# Revit family: GT_клапан
name_source: partatom
category: Арматура воздуховодов
revit_build: Autodesk Revit 2014 (Build: 20130308_1515(x64)
units: mm (PartAtom-declared; Revit-internal decimal feet)

## types (374) — shared parameters
T = 20 мм
URL = http://inplast.ru
Изготовитель = INPLAST-SMAY
Материал = Оцинкованная сталь (INPLAST)
Описание = Щелевой клапан расхода воздуха из оцинкованной стали
zero-valued in all types: Вес, кг

## per-type parameters (varying)
| type | Aef | C | D |
| GT-75х75 | 0.003 м² | 75 мм | 75 мм |
| GT-100х100 | 0.006 м² | 100 мм | 100 мм |
| GT-125х100 | 0.008 м² | 125 мм | 100 мм |
| GT-125х125 | 0.009 м² | 125 мм | 125 мм |
| GT-150х100 | 0.009 м² | 150 мм | 100 мм |
| GT-150х125 | 0.011 м² | 150 мм | 125 мм |
| GT-150х150 | 0.014 м² | 150 мм | 150 мм |
| GT-200х100 | 0.012 м² | 200 мм | 100 мм |
| GT-200х125 | 0.015 м² | 200 мм | 125 мм |
| GT-200х150 | 0.018 м² | 200 мм | 150 мм |
| GT-200х200 | 0.024 м² | 200 мм | 200 мм |
| GT-205х205 | 0.025 м² | 205 мм | 205 мм |
| GT-225х100 | 0.014 м² | 225 мм | 100 мм |
| GT-225х125 | 0.017 м² | 225 мм | 125 мм |
| GT-225х150 | 0.020 м² | 225 мм | 150 мм |
| GT-225х200 | 0.027 м² | 225 мм | 200 мм |
| GT-225х225 | 0.030 м² | 225 мм | 225 мм |
| GT-250х100 | 0.015 м² | 250 мм | 100 мм |
| GT-250х125 | 0.019 м² | 250 мм | 125 мм |
| GT-250х150 | 0.023 м² | 250 мм | 150 мм |
| GT-250х200 | 0.030 м² | 250 мм | 200 мм |
| GT-250х225 | 0.034 м² | 250 мм | 225 мм |
| GT-250х250 | 0.038 м² | 250 мм | 250 мм |
| GT-261х261 | 0.041 м² | 261 мм | 261 мм |
| GT-300х100 | 0.018 м² | 300 мм | 100 мм |
| GT-300х125 | 0.023 м² | 300 мм | 125 мм |
| GT-300х150 | 0.027 м² | 300 мм | 150 мм |
| GT-300х200 | 0.036 м² | 300 мм | 200 мм |
| GT-300х225 | 0.041 м² | 300 мм | 225 мм |
| GT-300х250 | 0.045 м² | 300 мм | 250 мм |
| GT-300х300 | 0.054 м² | 300 мм | 300 мм |
| GT-317х317 | 0.060 м² | 317 мм | 317 мм |
| GT-325х100 | 0.020 м² | 325 мм | 100 мм |
| GT-325х125 | 0.024 м² | 325 мм | 125 мм |
| GT-325х150 | 0.029 м² | 325 мм | 150 мм |
| GT-325х200 | 0.039 м² | 325 мм | 200 мм |
| GT-325х225 | 0.044 м² | 325 мм | 225 мм |
| GT-325х250 | 0.049 м² | 325 мм | 250 мм |
| GT-325х300 | 0.059 м² | 325 мм | 300 мм |
| GT-325х325 | 0.064 м² | 325 мм | 325 мм |
| GT-350х100 | 0.021 м² | 350 мм | 100 мм |
| GT-350х125 | 0.026 м² | 350 мм | 125 мм |
| GT-350х150 | 0.032 м² | 350 мм | 150 мм |
| GT-350х200 | 0.042 м² | 350 мм | 200 мм |
| GT-350х225 | 0.047 м² | 350 мм | 225 мм |
| GT-350х250 | 0.053 м² | 350 мм | 250 мм |
| GT-350х300 | 0.063 м² | 350 мм | 300 мм |
| GT-350х325 | 0.068 м² | 350 мм | 325 мм |
| GT-350х350 | 0.074 м² | 350 мм | 350 мм |
| GT-372х372 | 0.083 м² | 372 мм | 372 мм |
| GT-400х100 | 0.024 м² | 400 мм | 100 мм |
| GT-400х125 | 0.030 м² | 400 мм | 125 мм |
| GT-400х150 | 0.036 м² | 400 мм | 150 мм |
| GT-400х200 | 0.048 м² | 400 мм | 200 мм |
| GT-400х225 | 0.054 м² | 400 мм | 225 мм |
| GT-400х250 | 0.060 м² | 400 мм | 250 мм |
| GT-400х300 | 0.072 м² | 400 мм | 300 мм |
| GT-400х325 | 0.078 м² | 400 мм | 325 мм |
| GT-400х350 | 0.084 м² | 400 мм | 350 мм |
| GT-400х400 | 0.096 м² | 400 мм | 400 мм |
| GT-425х100 | 0.026 м² | 425 мм | 100 мм |
| GT-425х125 | 0.032 м² | 425 мм | 125 мм |
| GT-425х150 | 0.038 м² | 425 мм | 150 мм |
| GT-425х200 | 0.051 м² | 425 мм | 200 мм |
| GT-425х225 | 0.058 м² | 425 мм | 225 мм |
| GT-425х250 | 0.064 м² | 425 мм | 250 мм |
| GT-425х300 | 0.077 м² | 425 мм | 300 мм |
| GT-425х325 | 0.083 м² | 425 мм | 325 мм |
| GT-425х350 | 0.089 м² | 425 мм | 350 мм |
| GT-425х400 | 0.102 м² | 425 мм | 400 мм |
| GT-425х425 | 0.109 м² | 425 мм | 425 мм |
| GT-429х429 | 0.111 м² | 429 мм | 429 мм |
| GT-450х100 | 0.027 м² | 450 мм | 100 мм |
| GT-450х125 | 0.034 м² | 450 мм | 125 мм |
| GT-450х150 | 0.041 м² | 450 мм | 150 мм |
| GT-450х200 | 0.054 м² | 450 мм | 200 мм |
| GT-450х225 | 0.061 м² | 450 мм | 225 мм |
| GT-450х250 | 0.068 м² | 450 мм | 250 мм |
| GT-450х300 | 0.081 м² | 450 мм | 300 мм |
| GT-450х325 | 0.088 м² | 450 мм | 325 мм |
| GT-450х350 | 0.095 м² | 450 мм | 350 мм |
| GT-450х400 | 0.108 м² | 450 мм | 400 мм |
| GT-450х425 | 0.115 м² | 450 мм | 425 мм |
| GT-450х450 | 0.122 м² | 450 мм | 450 мм |
| GT-458х458 | 0.126 м² | 458 мм | 458 мм |
| GT-500х100 | 0.030 м² | 500 мм | 100 мм |
| GT-500х125 | 0.038 м² | 500 мм | 125 мм |
| GT-500х150 | 0.045 м² | 500 мм | 150 мм |
| GT-500х200 | 0.060 м² | 500 мм | 200 мм |
| GT-500х225 | 0.068 м² | 500 мм | 225 мм |
| GT-500х250 | 0.075 м² | 500 мм | 250 мм |
| GT-500х300 | 0.090 м² | 500 мм | 300 мм |
| GT-500х325 | 0.098 м² | 500 мм | 325 мм |
| GT-500х350 | 0.105 м² | 500 мм | 350 мм |
| GT-500х400 | 0.120 м² | 500 мм | 400 мм |
| GT-500х425 | 0.128 м² | 500 мм | 425 мм |
| GT-500х450 | 0.135 м² | 500 мм | 450 мм |
| GT-500х500 | 0.150 м² | 500 мм | 500 мм |
| GT-525х100 | 0.032 м² | 525 мм | 100 мм |
| GT-525х125 | 0.039 м² | 525 мм | 125 мм |
| GT-525х150 | 0.047 м² | 525 мм | 150 мм |
| GT-525х200 | 0.063 м² | 525 мм | 200 мм |
| GT-525х225 | 0.071 м² | 525 мм | 225 мм |
| GT-525х250 | 0.079 м² | 525 мм | 250 мм |
| GT-525х300 | 0.095 м² | 525 мм | 300 мм |
| GT-525х325 | 0.103 м² | 525 мм | 325 мм |
| GT-525х350 | 0.111 м² | 525 мм | 350 мм |
| GT-525х400 | 0.126 м² | 525 мм | 400 мм |
| GT-525х425 | 0.134 м² | 525 мм | 425 мм |
| GT-525х450 | 0.142 м² | 525 мм | 450 мм |
| GT-525х500 | 0.158 м² | 525 мм | 500 мм |
| GT-525х525 | 0.166 м² | 525 мм | 525 мм |
| GT-550х100 | 0.033 м² | 550 мм | 100 мм |
| GT-550х125 | 0.041 м² | 550 мм | 125 мм |
| GT-550х150 | 0.050 м² | 550 мм | 150 мм |
| GT-550х200 | 0.066 м² | 550 мм | 200 мм |
| GT-550х225 | 0.074 м² | 550 мм | 225 мм |
| GT-550х250 | 0.083 м² | 550 мм | 250 мм |
| GT-550х300 | 0.099 м² | 550 мм | 300 мм |
| GT-550х325 | 0.108 м² | 550 мм | 325 мм |
| GT-550х350 | 0.116 м² | 550 мм | 350 мм |
| GT-550х400 | 0.132 м² | 550 мм | 400 мм |
| GT-550х425 | 0.141 м² | 550 мм | 425 мм |
| GT-550х450 | 0.149 м² | 550 мм | 450 мм |
| GT-550х500 | 0.165 м² | 550 мм | 500 мм |
| GT-550х525 | 0.174 м² | 550 мм | 525 мм |
| GT-550х550 | 0.182 м² | 550 мм | 550 мм |
| GT-558х558 | 0.187 м² | 558 мм | 558 мм |
| GT-586х586 | 0.207 м² | 586 мм | 586 мм |
| GT-600х100 | 0.036 м² | 600 мм | 100 мм |
| GT-600х125 | 0.045 м² | 600 мм | 125 мм |
| GT-600х150 | 0.054 м² | 600 мм | 150 мм |
| GT-600х200 | 0.072 м² | 600 мм | 200 мм |
| GT-600х225 | 0.081 м² | 600 мм | 225 мм |
| GT-600х250 | 0.090 м² | 600 мм | 250 мм |
| GT-600х300 | 0.108 м² | 600 мм | 300 мм |
| GT-600х325 | 0.117 м² | 600 мм | 325 мм |
| GT-600х350 | 0.126 м² | 600 мм | 350 мм |
| GT-600х400 | 0.144 м² | 600 мм | 400 мм |
| GT-600х425 | 0.153 м² | 600 мм | 425 мм |
| GT-600х450 | 0.162 м² | 600 мм | 450 мм |
| GT-600х500 | 0.180 м² | 600 мм | 500 мм |
| GT-600х525 | 0.190 м² | 600 мм | 525 мм |
| GT-600х550 | 0.199 м² | 600 мм | 550 мм |
| GT-600х600 | 0.217 м² | 600 мм | 600 мм |
| GT-625х100 | 0.038 м² | 625 мм | 100 мм |
| GT-625х125 | 0.047 м² | 625 мм | 125 мм |
| GT-625х150 | 0.056 м² | 625 мм | 150 мм |
| GT-625х200 | 0.075 м² | 625 мм | 200 мм |
| GT-625х225 | 0.085 м² | 625 мм | 225 мм |
| GT-625х250 | 0.094 м² | 625 мм | 250 мм |
| GT-625х300 | 0.113 м² | 625 мм | 300 мм |
| GT-625х325 | 0.122 м² | 625 мм | 325 мм |
| GT-625х350 | 0.132 м² | 625 мм | 350 мм |
| GT-625х400 | 0.150 м² | 625 мм | 400 мм |
| GT-625х425 | 0.160 м² | 625 мм | 425 мм |
| GT-625х450 | 0.169 м² | 625 мм | 450 мм |
| GT-625х500 | 0.188 м² | 625 мм | 500 мм |
| GT-625х525 | 0.197 м² | 625 мм | 525 мм |
| GT-625х550 | 0.207 м² | 625 мм | 550 мм |
| GT-625х600 | 0.226 м² | 625 мм | 600 мм |
| GT-625х625 | 0.235 м² | 625 мм | 625 мм |
| GT-650х100 | 0.039 м² | 650 мм | 100 мм |
| GT-650х125 | 0.049 м² | 650 мм | 125 мм |
| GT-650х150 | 0.059 м² | 650 мм | 150 мм |
| GT-650х200 | 0.078 м² | 650 мм | 200 мм |
| GT-650х225 | 0.088 м² | 650 мм | 225 мм |
| GT-650х250 | 0.098 м² | 650 мм | 250 мм |
| GT-650х300 | 0.117 м² | 650 мм | 300 мм |
| GT-650х325 | 0.127 м² | 650 мм | 325 мм |
| GT-650х350 | 0.137 м² | 650 мм | 350 мм |
| GT-650х400 | 0.156 м² | 650 мм | 400 мм |
| GT-650х425 | 0.166 м² | 650 мм | 425 мм |
| GT-650х450 | 0.176 м² | 650 мм | 450 мм |
| GT-650х500 | 0.196 м² | 650 мм | 500 мм |
| GT-650х525 | 0.205 м² | 650 мм | 525 мм |
| GT-650х550 | 0.215 м² | 650 мм | 550 мм |
| GT-650х600 | 0.235 м² | 650 мм | 600 мм |
| GT-650х625 | 0.244 м² | 650 мм | 625 мм |
| GT-650х650 | 0.254 м² | 650 мм | 650 мм |
| GT-700х100 | 0.042 м² | 700 мм | 100 мм |
| GT-700х125 | 0.053 м² | 700 мм | 125 мм |
| GT-700х150 | 0.063 м² | 700 мм | 150 мм |
| GT-700х200 | 0.084 м² | 700 мм | 200 мм |
| GT-700х225 | 0.095 м² | 700 мм | 225 мм |
| GT-700х250 | 0.105 м² | 700 мм | 250 мм |
| GT-700х300 | 0.126 м² | 700 мм | 300 мм |
| GT-700х325 | 0.137 м² | 700 мм | 325 мм |
| GT-700х350 | 0.147 м² | 700 мм | 350 мм |
| GT-700х400 | 0.168 м² | 700 мм | 400 мм |
| GT-700х425 | 0.179 м² | 700 мм | 425 мм |
| GT-700х450 | 0.190 м² | 700 мм | 450 мм |
| GT-700х500 | 0.211 м² | 700 мм | 500 мм |
| GT-700х525 | 0.221 м² | 700 мм | 525 мм |
| GT-700х550 | 0.232 м² | 700 мм | 550 мм |
| GT-700х600 | 0.253 м² | 700 мм | 600 мм |
| GT-700х625 | 0.263 м² | 700 мм | 625 мм |
| GT-700х650 | 0.274 м² | 700 мм | 650 мм |
| GT-725х100 | 0.044 м² | 725 мм | 100 мм |
| GT-725х125 | 0.055 м² | 725 мм | 125 мм |
| GT-725х150 | 0.065 м² | 725 мм | 150 мм |
| GT-725х200 | 0.087 м² | 725 мм | 200 мм |
| GT-725х225 | 0.098 м² | 725 мм | 225 мм |
| GT-725х250 | 0.109 м² | 725 мм | 250 мм |
| GT-725х300 | 0.131 м² | 725 мм | 300 мм |
| GT-725х325 | 0.142 м² | 725 мм | 325 мм |
| GT-725х350 | 0.153 м² | 725 мм | 350 мм |
| GT-725х400 | 0.174 м² | 725 мм | 400 мм |
| GT-725х425 | 0.185 м² | 725 мм | 425 мм |
| GT-725х450 | 0.196 м² | 725 мм | 450 мм |
| GT-725х500 | 0.218 м² | 725 мм | 500 мм |
| GT-725х525 | 0.229 м² | 725 мм | 525 мм |
| GT-725х550 | 0.240 м² | 725 мм | 550 мм |
| GT-725х600 | 0.262 м² | 725 мм | 600 мм |
| GT-725х625 | 0.273 м² | 725 мм | 625 мм |
| GT-725х650 | 0.284 м² | 725 мм | 650 мм |
| GT-750х100 | 0.045 м² | 750 мм | 100 мм |
| GT-750х125 | 0.056 м² | 750 мм | 125 мм |
| GT-750х150 | 0.068 м² | 750 мм | 150 мм |
| GT-750х200 | 0.090 м² | 750 мм | 200 мм |
| GT-750х225 | 0.102 м² | 750 мм | 225 мм |
| GT-750х250 | 0.113 м² | 750 мм | 250 мм |
| GT-750х300 | 0.135 м² | 750 мм | 300 мм |
| GT-750х325 | 0.147 м² | 750 мм | 325 мм |
| GT-750х350 | 0.158 м² | 750 мм | 350 мм |
| GT-750х400 | 0.180 м² | 750 мм | 400 мм |
| GT-750х425 | 0.192 м² | 750 мм | 425 мм |
| GT-750х450 | 0.203 м² | 750 мм | 450 мм |
| GT-750х500 | 0.226 м² | 750 мм | 500 мм |
| GT-750х525 | 0.237 м² | 750 мм | 525 мм |
| GT-750х550 | 0.248 м² | 750 мм | 550 мм |
| GT-750х600 | 0.271 м² | 750 мм | 600 мм |
| GT-750х625 | 0.282 м² | 750 мм | 625 мм |
| GT-750х650 | 0.293 м² | 750 мм | 650 мм |
| GT-800х100 | 0.048 м² | 800 мм | 100 мм |
| GT-800х125 | 0.060 м² | 800 мм | 125 мм |
| GT-800х150 | 0.072 м² | 800 мм | 150 мм |
| GT-800х200 | 0.096 м² | 800 мм | 200 мм |
| GT-800х225 | 0.108 м² | 800 мм | 225 мм |
| GT-800х250 | 0.120 м² | 800 мм | 250 мм |
| GT-800х300 | 0.144 м² | 800 мм | 300 мм |
| GT-800х325 | 0.156 м² | 800 мм | 325 мм |
| GT-800х350 | 0.168 м² | 800 мм | 350 мм |
| GT-800х400 | 0.193 м² | 800 мм | 400 мм |
| GT-800х425 | 0.205 м² | 800 мм | 425 мм |
| GT-800х450 | 0.217 м² | 800 мм | 450 мм |
| GT-800х500 | 0.241 м² | 800 мм | 500 мм |
| GT-800х525 | 0.253 м² | 800 мм | 525 мм |
| GT-800х550 | 0.265 м² | 800 мм | 550 мм |
| GT-800х600 | 0.289 м² | 800 мм | 600 мм |
| GT-800х625 | 0.301 м² | 800 мм | 625 мм |
| GT-800х650 | 0.313 м² | 800 мм | 650 мм |
| GT-825х100 | 0.050 м² | 825 мм | 100 мм |
| GT-825х125 | 0.062 м² | 825 мм | 125 мм |
| GT-825х150 | 0.074 м² | 825 мм | 150 мм |
| GT-825х200 | 0.099 м² | 825 мм | 200 мм |
| GT-825х225 | 0.112 м² | 825 мм | 225 мм |
| GT-825х250 | 0.124 м² | 825 мм | 250 мм |
| GT-825х300 | 0.149 м² | 825 мм | 300 мм |
| GT-825х325 | 0.161 м² | 825 мм | 325 мм |
| GT-825х350 | 0.174 м² | 825 мм | 350 мм |
| GT-825х400 | 0.199 м² | 825 мм | 400 мм |
| GT-825х425 | 0.211 м² | 825 мм | 425 мм |
| GT-825х450 | 0.223 м² | 825 мм | 450 мм |
| GT-825х500 | 0.248 м² | 825 мм | 500 мм |
| GT-825х525 | 0.261 м² | 825 мм | 525 мм |
| GT-825х550 | 0.273 м² | 825 мм | 550 мм |
| GT-825х600 | 0.298 м² | 825 мм | 600 мм |
| GT-825х625 | 0.310 м² | 825 мм | 625 мм |
| GT-825х650 | 0.323 м² | 825 мм | 650 мм |
| GT-850х100 | 0.051 м² | 850 мм | 100 мм |
| GT-850х125 | 0.064 м² | 850 мм | 125 мм |
| GT-850х150 | 0.077 м² | 850 мм | 150 мм |
| GT-850х200 | 0.102 м² | 850 мм | 200 мм |
| GT-850х225 | 0.115 м² | 850 мм | 225 мм |
| GT-850х250 | 0.128 м² | 850 мм | 250 мм |
| GT-850х300 | 0.153 м² | 850 мм | 300 мм |
| GT-850х325 | 0.166 м² | 850 мм | 325 мм |
| GT-850х350 | 0.179 м² | 850 мм | 350 мм |
| GT-850х400 | 0.205 м² | 850 мм | 400 мм |
| GT-850х425 | 0.217 м² | 850 мм | 425 мм |
| GT-850х450 | 0.230 м² | 850 мм | 450 мм |
| GT-850х500 | 0.256 м² | 850 мм | 500 мм |
| GT-850х525 | 0.268 м² | 850 мм | 525 мм |
| GT-850х550 | 0.281 м² | 850 мм | 550 мм |
| GT-850х600 | 0.307 м² | 850 мм | 600 мм |
| GT-850х625 | 0.320 м² | 850 мм | 625 мм |
| GT-850х650 | 0.332 м² | 850 мм | 650 мм |
| GT-900х100 | 0.054 м² | 900 мм | 100 мм |
| GT-900х125 | 0.068 м² | 900 мм | 125 мм |
| GT-900х150 | 0.081 м² | 900 мм | 150 мм |
| GT-900х200 | 0.108 м² | 900 мм | 200 мм |
| GT-900х225 | 0.122 м² | 900 мм | 225 мм |
| GT-900х250 | 0.135 м² | 900 мм | 250 мм |
| GT-900х300 | 0.162 м² | 900 мм | 300 мм |
| GT-900х325 | 0.176 м² | 900 мм | 325 мм |
| GT-900х350 | 0.190 м² | 900 мм | 350 мм |
| GT-900х400 | 0.217 м² | 900 мм | 400 мм |
| GT-900х425 | 0.230 м² | 900 мм | 425 мм |
| GT-900х450 | 0.244 м² | 900 мм | 450 мм |
| GT-900х500 | 0.271 м² | 900 мм | 500 мм |
| GT-900х525 | 0.284 м² | 900 мм | 525 мм |
| GT-900х550 | 0.298 м² | 900 мм | 550 мм |
| GT-900х600 | 0.325 м² | 900 мм | 600 мм |
| GT-900х625 | 0.338 м² | 900 мм | 625 мм |
| GT-900х650 | 0.352 м² | 900 мм | 650 мм |
| GT-925х100 | 0.056 м² | 925 мм | 100 мм |
| GT-925х125 | 0.070 м² | 925 мм | 125 мм |
| GT-925х150 | 0.083 м² | 925 мм | 150 мм |
| GT-925х200 | 0.111 м² | 925 мм | 200 мм |
| GT-925х225 | 0.125 м² | 925 мм | 225 мм |
| GT-925х250 | 0.139 м² | 925 мм | 250 мм |
| GT-925х300 | 0.167 м² | 925 мм | 300 мм |
| GT-925х325 | 0.181 м² | 925 мм | 325 мм |
| GT-925х350 | 0.195 м² | 925 мм | 350 мм |
| GT-925х400 | 0.223 м² | 925 мм | 400 мм |
| GT-925х425 | 0.237 м² | 925 мм | 425 мм |
| GT-925х450 | 0.250 м² | 925 мм | 450 мм |
| GT-925х500 | 0.278 м² | 925 мм | 500 мм |
| GT-925х525 | 0.292 м² | 925 мм | 525 мм |
| GT-925х550 | 0.306 м² | 925 мм | 550 мм |
| GT-925х600 | 0.334 м² | 925 мм | 600 мм |
| GT-925х625 | 0.348 м² | 925 мм | 625 мм |
| GT-925х650 | 0.362 м² | 925 мм | 650 мм |
| GT-950х100 | 0.057 м² | 950 мм | 100 мм |
| GT-950х125 | 0.071 м² | 950 мм | 125 мм |
| GT-950х150 | 0.086 м² | 950 мм | 150 мм |
| GT-950х200 | 0.114 м² | 950 мм | 200 мм |
| GT-950х225 | 0.129 м² | 950 мм | 225 мм |
| GT-950х250 | 0.143 м² | 950 мм | 250 мм |
| GT-950х300 | 0.171 м² | 950 мм | 300 мм |
| GT-950х325 | 0.186 м² | 950 мм | 325 мм |
| GT-950х350 | 0.200 м² | 950 мм | 350 мм |
| GT-950х400 | 0.229 м² | 950 мм | 400 мм |
| GT-950х425 | 0.243 м² | 950 мм | 425 мм |
| GT-950х450 | 0.257 м² | 950 мм | 450 мм |
| GT-950х500 | 0.286 м² | 950 мм | 500 мм |
| GT-950х525 | 0.300 м² | 950 мм | 525 мм |
| GT-950х550 | 0.314 м² | 950 мм | 550 мм |
| GT-950х600 | 0.343 м² | 950 мм | 600 мм |
| GT-950х625 | 0.357 м² | 950 мм | 625 мм |
| GT-950х650 | 0.371 м² | 950 мм | 650 мм |
| GT-1000х100 | 0.060 м² | 1000 мм | 100 мм |
| GT-1000х125 | 0.075 м² | 1000 мм | 125 мм |
| GT-1000х150 | 0.090 м² | 1000 мм | 150 мм |
| GT-1000х200 | 0.120 м² | 1000 мм | 200 мм |
| GT-1000х225 | 0.135 м² | 1000 мм | 225 мм |
| GT-1000х250 | 0.150 м² | 1000 мм | 250 мм |
| GT-1000х300 | 0.180 м² | 1000 мм | 300 мм |
| GT-1000х325 | 0.196 м² | 1000 мм | 325 мм |
| GT-1000х350 | 0.211 м² | 1000 мм | 350 мм |
| GT-1000х400 | 0.241 м² | 1000 мм | 400 мм |
| GT-1000х425 | 0.256 м² | 1000 мм | 425 мм |
| GT-1000х450 | 0.271 м² | 1000 мм | 450 мм |
| GT-1000х500 | 0.301 м² | 1000 мм | 500 мм |
| GT-1000х525 | 0.316 м² | 1000 мм | 525 мм |
| GT-1000х550 | 0.331 м² | 1000 мм | 550 мм |
| GT-1000х600 | 0.361 м² | 1000 мм | 600 мм |
| GT-1000х625 | 0.376 м² | 1000 мм | 625 мм |
| GT-1000х650 | 0.391 м² | 1000 мм | 650 мм |
| GT-1025х100 | 0.062 м² | 1025 мм | 100 мм |
| GT-1025х125 | 0.077 м² | 1025 мм | 125 мм |
| GT-1025х150 | 0.092 м² | 1025 мм | 150 мм |
| GT-1025х200 | 0.123 м² | 1025 мм | 200 мм |
| GT-1025х225 | 0.139 м² | 1025 мм | 225 мм |
| GT-1025х250 | 0.154 м² | 1025 мм | 250 мм |
| GT-1025х300 | 0.185 м² | 1025 мм | 300 мм |
| GT-1025х325 | 0.200 м² | 1025 мм | 325 мм |
| GT-1025х350 | 0.216 м² | 1025 мм | 350 мм |
| GT-1025х400 | 0.247 м² | 1025 мм | 400 мм |
| GT-1025х425 | 0.262 м² | 1025 мм | 425 мм |
| GT-1025х450 | 0.277 м² | 1025 мм | 450 мм |
| GT-1025х500 | 0.308 м² | 1025 мм | 500 мм |
| GT-1025х525 | 0.324 м² | 1025 мм | 525 мм |

note: column(s) folded — value = type name in every type: Комментарии к типоразмеру
